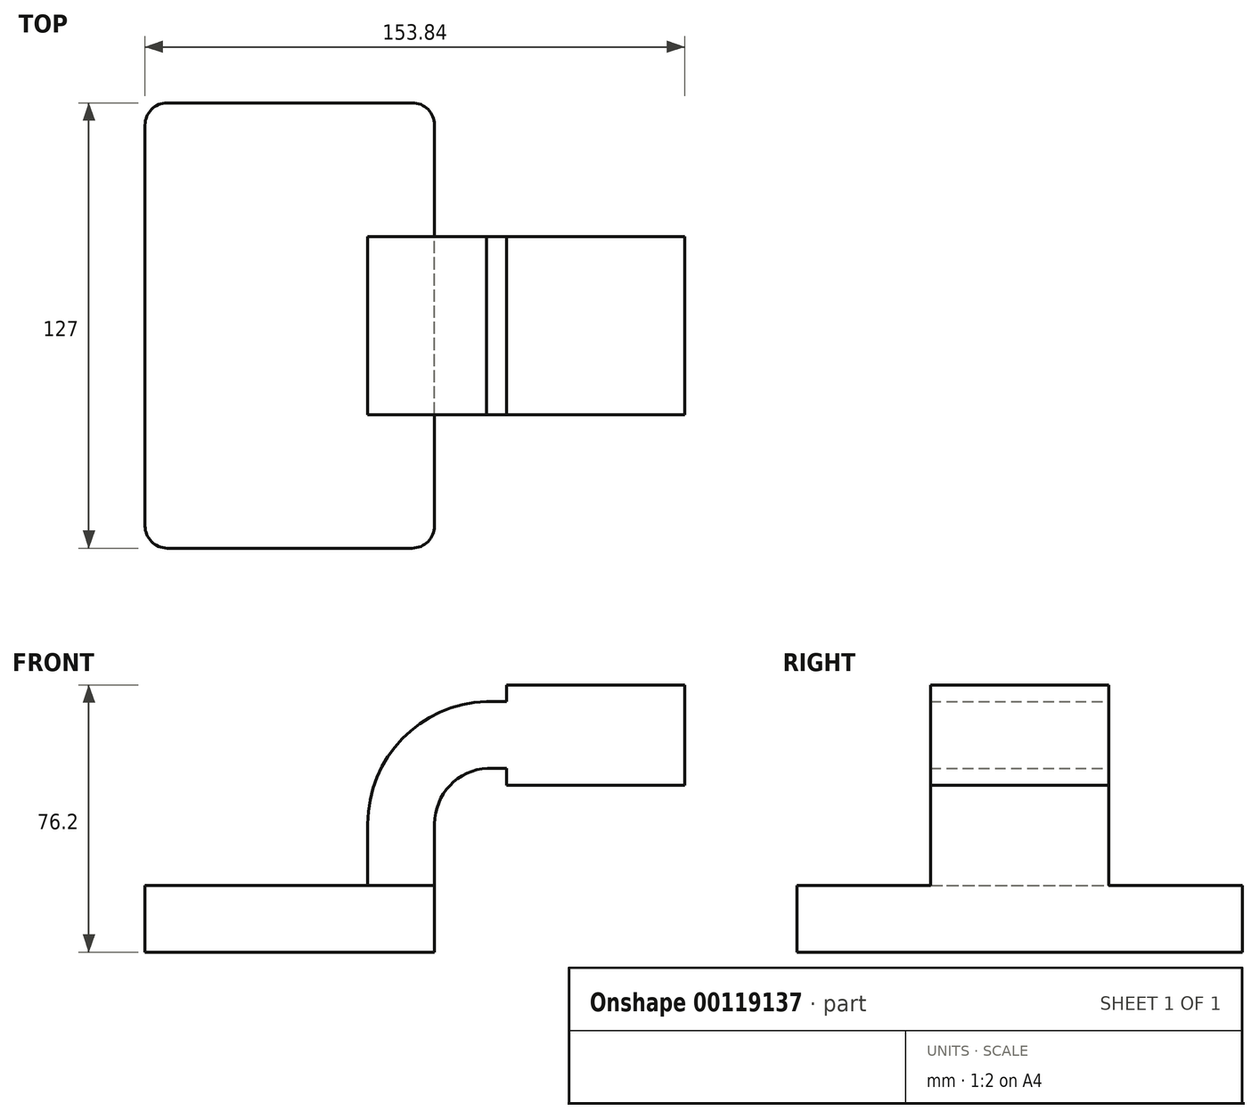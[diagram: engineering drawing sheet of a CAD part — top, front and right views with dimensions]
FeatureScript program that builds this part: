
annotation { "Feature Type Name" : "Feature", "Feature Type Description" : "" }
export const myFeature = defineFeature(function(context is Context, id is Id, definition is map)
    precondition{}
    {
        {
            var Q0;
            Q0=qCreatedBy(makeId("Front.planeOp"),FACE);
            var sketch = newSketch(context, id + "F0", { "sketchPlane" : qUnion([Q0])});
            skLineSegment(sketch, "E0.bottom", {"start": v(41.27, 9.53) * mm, "end": v(-41.28, 9.53) * mm});
            skLineSegment(sketch, "E0.top", {"start": v(41.28, -9.52) * mm, "end": v(-41.27, -9.52) * mm});
            skLineSegment(sketch, "E0.left", {"start": v(41.28, 9.53) * mm, "end": v(41.28, -9.52) * mm});
            skLineSegment(sketch, "E0.right", {"start": v(-41.28, 9.53) * mm, "end": v(-41.27, -9.52) * mm});
            skPoint(sketch, "E0.middle", {"position": v(0, 0) * mm});
            skLineSegment(sketch, "E1", {"start": v(41.27, 9.53) * mm, "end": v(41.27, 27.02) * mm});
            skLineSegment(sketch, "E2.bottom", {"start": v(112.57, 38.1) * mm, "end": v(61.77, 38.1) * mm});
            skLineSegment(sketch, "E2.top", {"start": v(112.57, 66.68) * mm, "end": v(61.77, 66.68) * mm});
            skLineSegment(sketch, "E2.left", {"start": v(112.57, 38.1) * mm, "end": v(112.57, 66.68) * mm});
            skLineSegment(sketch, "E2.right", {"start": v(61.77, 38.1) * mm, "end": v(61.77, 66.68) * mm});
            skPoint(sketch, "E2.middle", {"position": v(87.17, 52.39) * mm});
            skArc(sketch, "E3", {"start": v(41.27, 27.02) * mm, "mid": v(45.66, 37.98) * mm, "end": v(56.4, 42.88) * mm});
            skLineSegment(sketch, "E4", {"start": v(56.4, 42.88) * mm, "end": v(73.55, 42.88) * mm});
            skLineSegment(sketch, "E5.0", {"start": v(56.04, 61.93) * mm, "end": v(73.55, 61.93) * mm});
            skArc(sketch, "E5.1", {"start": v(22.22, 27.02) * mm, "mid": v(32.06, 51.32) * mm, "end": v(56.04, 61.93) * mm});
            skLineSegment(sketch, "E5.2", {"start": v(22.22, 9.53) * mm, "end": v(22.22, 27.02) * mm});
            skLineSegment(sketch, "E6", {"start": v(73.55, 61.93) * mm, "end": v(73.55, 42.88) * mm});
            skFitSpline(sketch, "E7", {"points": [v(-41.28, 9.53) * mm, v(56.04, 61.93) * mm], "startDerivative": vector(53.38, 136.53) * mm, "endDerivative": vector(143.6, -1.46) * mm});
            skLineSegment(sketch, "E8", {"start": v(87.17, 52.39) * mm, "end": v(87.17, 66.68) * mm});
            skLineSegment(sketch, "E9", {"start": v(87.17, 52.39) * mm, "end": v(87.17, 38.1) * mm});
            skSolve(sketch);
        }
        {
            var Q0;
            Q0=makeQuery(id+"F0.imprint","IMPRINT",FACE,{"disambiguationData":[TD([[makeQuery(id+"F0.imprint","IMPRINT",EDGE,{"derivedFrom":sQuery(id+"F0.wireOp",EDGE,"E0.top")}),-1.0]])]});
            extrude(context, id + "F1", {"entities" : qUnion([Q0]), "endBound" : BoundingType.SYMMETRIC, "depth" : 127 * mm});
        }
        {
            var Q0;
            {var subQ1=sQuery(id+"F0.wireOp",EDGE,"E1");Q0=makeQuery(id+"F0.imprint","IMPRINT",FACE,{"disambiguationData":[TD([[makeQuery(id+"F0.imprint","IMPRINT",EDGE,{"derivedFrom":subQ1}),1.0]])]});}
            var Q1;
            {var subQ1=sQuery(id+"F0.wireOp",EDGE,"E2.bottom");Q1=makeQuery(id+"F0.imprint","IMPRINT",FACE,{"disambiguationData":[TD([[makeQuery(id+"F0.imprint","IMPRINT",EDGE,{"derivedFrom":subQ1}),-1.0]])]});}
            var Q2;
            {var subQ5=sQuery(id+"F0.wireOp",EDGE,"E6");Q2=makeQuery(id+"F0.imprint","IMPRINT",FACE,{"disambiguationData":[TD([[makeQuery(id+"F0.imprint","IMPRINT",EDGE,{"derivedFrom":subQ5}),-1.0]])]});}
            var Q3;
            {var subQ11=sQuery(id+"F0.wireOp",EDGE,"E6");Q3=makeQuery(id+"F0.imprint","IMPRINT",FACE,{"disambiguationData":[TD([[makeQuery(id+"F0.imprint","IMPRINT",EDGE,{"derivedFrom":subQ11}),1.0]])]});}
            extrude(context, id + "F2", {"entities" : qUnion([Q0, Q1, Q2, Q3]), "operationType" : NewBodyOperationType.ADD, "endBound" : BoundingType.SYMMETRIC, "depth" : 50.8 * mm});
        }
        {
            var Q0;
            Q0=makeQuery(id+"F0.imprint","IMPRINT",FACE,{"disambiguationData":[TD([[makeQuery(id+"F0.imprint","IMPRINT",EDGE,{"derivedFrom":sQuery(id+"F0.wireOp",EDGE,"E5.1")}),1.0]])]});
            extrude(context, id + "F3", {"entities" : qUnion([Q0]), "operationType" : NewBodyOperationType.ADD, "endBound" : BoundingType.SYMMETRIC, "depth" : 15.88 * mm});
        }
        {
            var Q0;
            Q0=makeQuery(id+"F1.opExtrude","CAP_EDGE",EDGE,{"disambiguationData":[OSD([sQuery(id+"F0.wireOp",EDGE,"E0.left")])],"isStart":false});
            var Q1;
            Q1=makeQuery(id+"F1.opExtrude","CAP_EDGE",EDGE,{"disambiguationData":[OSD([sQuery(id+"F0.wireOp",EDGE,"E0.left")])],"isStart":true});
            var Q2;
            Q2=makeQuery(id+"F1.opExtrude","CAP_EDGE",EDGE,{"disambiguationData":[OSD([sQuery(id+"F0.wireOp",EDGE,"E0.right")])],"isStart":false});
            var Q3;
            Q3=makeQuery(id+"F1.opExtrude","CAP_EDGE",EDGE,{"disambiguationData":[OSD([sQuery(id+"F0.wireOp",EDGE,"E0.right")])],"isStart":true});
            fillet(context, id + "F4", {"entities" : qUnion([Q0, Q1, Q2, Q3]), "radius" : 6.35 * mm, "tangentPropagation" : true, "allowEdgeOverflow" : false});
        }
    });
